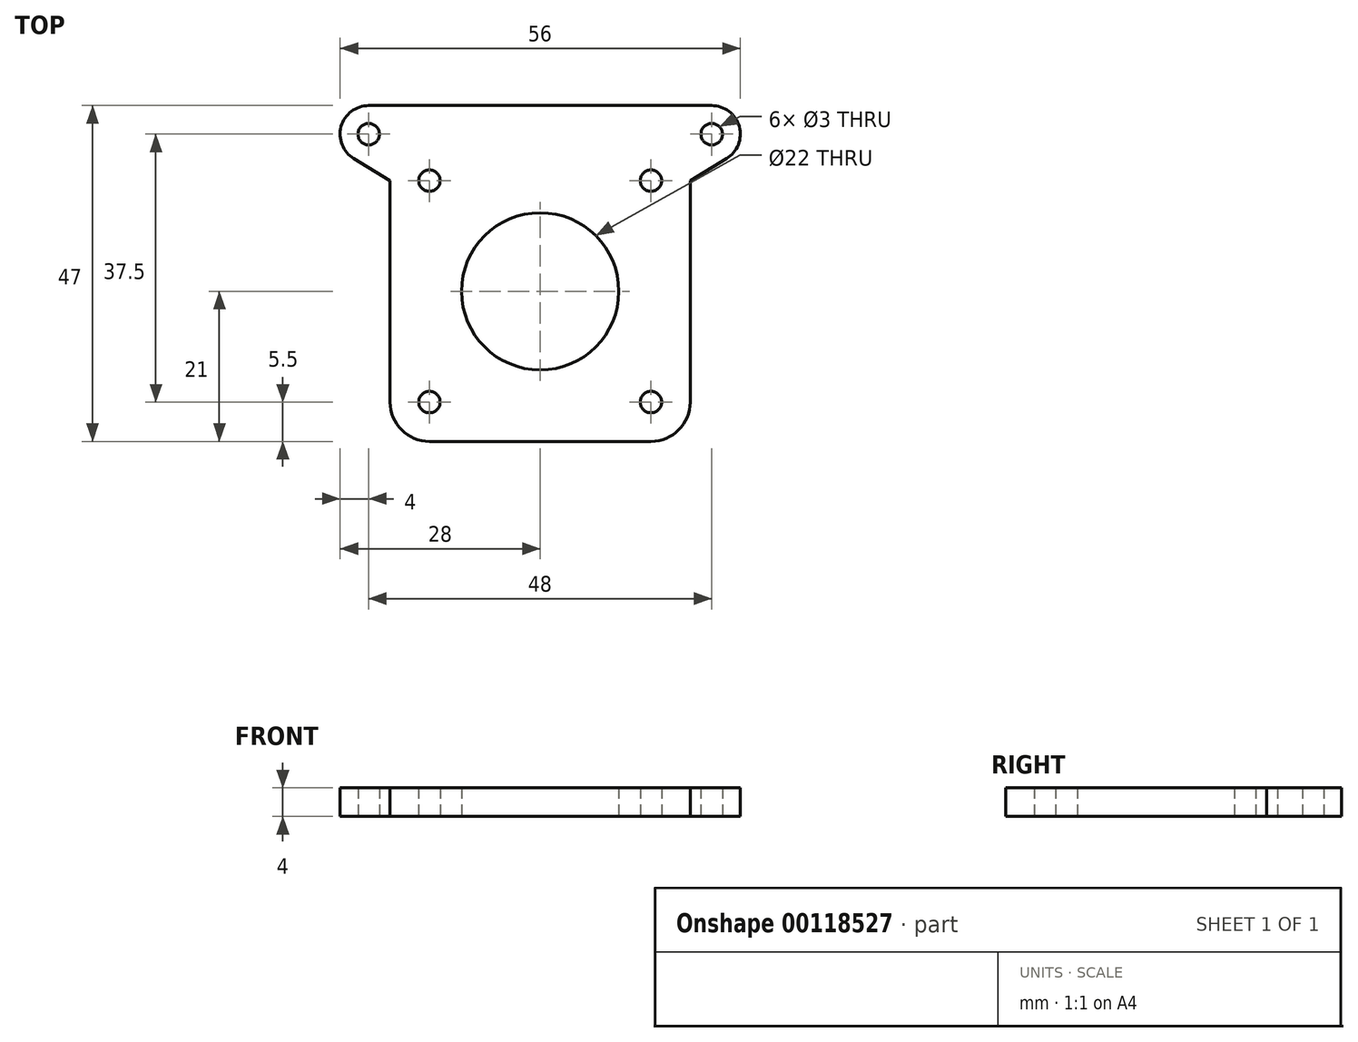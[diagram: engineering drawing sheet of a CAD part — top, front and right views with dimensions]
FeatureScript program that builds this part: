
annotation { "Feature Type Name" : "Feature", "Feature Type Description" : "" }
export const myFeature = defineFeature(function(context is Context, id is Id, definition is map)
    precondition{}
    {
        {
            var Q0;
            Q0=qCreatedBy(makeId("Top.planeOp"),FACE);
            var sketch = newSketch(context, id + "F0", { "sketchPlane" : qUnion([Q0])});
            skLineSegment(sketch, "E0.bottom", {"start": v(-15.5, 15.5) * mm, "end": v(15.5, 15.5) * mm, "construction": true});
            skLineSegment(sketch, "E0.top", {"start": v(-15.5, -15.5) * mm, "end": v(15.5, -15.5) * mm, "construction": true});
            skLineSegment(sketch, "E0.left", {"start": v(-15.5, 15.5) * mm, "end": v(-15.5, -15.5) * mm, "construction": true});
            skLineSegment(sketch, "E0.right", {"start": v(15.5, 15.5) * mm, "end": v(15.5, -15.5) * mm, "construction": true});
            skPoint(sketch, "E0.middle", {"position": v(0, 0) * mm});
            skCircle(sketch, "E1", {"center": v(-15.5, 15.5) * mm, "radius": 1.5 * mm});
            skCircle(sketch, "E2", {"center": v(15.5, 15.5) * mm, "radius": 1.5 * mm});
            skCircle(sketch, "E3", {"center": v(15.5, -15.5) * mm, "radius": 1.5 * mm});
            skCircle(sketch, "E4", {"center": v(-15.5, -15.5) * mm, "radius": 1.5 * mm});
            skCircle(sketch, "E5", {"center": v(0, 0) * mm, "radius": 11 * mm});
            skLineSegment(sketch, "E6.top", {"start": v(-15.5, -21) * mm, "end": v(15.5, -21) * mm});
            skLineSegment(sketch, "E6.left", {"start": v(-21, 15.5) * mm, "end": v(-21, -15.5) * mm});
            skLineSegment(sketch, "E6.right", {"start": v(21, 15.5) * mm, "end": v(21, -15.5) * mm});
            skPoint(sketch, "E7.visualSharp", {"position": v(-21, -21) * mm});
            skArc(sketch, "E7.filletArc", {"start": v(-21, -15.5) * mm, "mid": v(-19.39, -19.39) * mm, "end": v(-15.5, -21) * mm});
            skPoint(sketch, "E8.visualSharp", {"position": v(21, -21) * mm});
            skArc(sketch, "E8.filletArc", {"start": v(15.5, -21) * mm, "mid": v(19.39, -19.39) * mm, "end": v(21, -15.5) * mm});
            skCircle(sketch, "E9", {"center": v(-24, 22) * mm, "radius": 1.5 * mm});
            skCircle(sketch, "E10", {"center": v(24, 22) * mm, "radius": 1.5 * mm});
            skArc(sketch, "E11", {"start": v(-24, 26) * mm, "mid": v(-27.85, 23.08) * mm, "end": v(-26.08, 18.58) * mm});
            skArc(sketch, "E12", {"start": v(26.08, 18.58) * mm, "mid": v(27.85, 23.08) * mm, "end": v(24, 26) * mm});
            skLineSegment(sketch, "E13", {"start": v(-24, 26) * mm, "end": v(24, 26) * mm});
            skLineSegment(sketch, "E14", {"start": v(-21, 15.5) * mm, "end": v(-26.08, 18.58) * mm});
            skLineSegment(sketch, "E15", {"start": v(21, 15.5) * mm, "end": v(26.08, 18.58) * mm});
            skSolve(sketch);
        }
        {
            var Q0;
            Q0=makeQuery(id+"F0.imprint","IMPRINT",FACE,{"disambiguationData":[TD([[makeQuery(id+"F0.imprint","IMPRINT",EDGE,{"derivedFrom":sQuery(id+"F0.wireOp",EDGE,"E1")}),-1.0]])]});
            extrude(context, id + "F1", {"entities" : qUnion([Q0]), "depth" : 4 * mm});
        }
    });
